# Revit family: Mirror-Acorn-LR1812-SLPT
name_source: partatom
category: Generic Models
units: mm (PartAtom-declared; Revit-internal decimal feet)

## family parameters
Can host rebar = No
Cut with Voids When Loaded = No
Host = Face
OmniClass Number = 23.40.95.17.17
OmniClass Title = Mirrors
Part Type = Normal
Room Calculation Point = No
Round Connector Dimension = Use Diameter
Shared = Yes

## types (1)
- LR1812-SLPT
    ADA Compliant = Yes
    Assembly Code = E2010
    Default Elevation = 0"
    Description = Secur-Care® Ligature-Resistant, Stainless Steel Security Mirror
    EG - Enviro-Glaze = No
    Finish = Stainless Steel-Acorn-Satin
    Height = 23 3/8"
    Installation Type = Wall Mounted
    Length = 13"
    Manufacturer = Acorn Engineering
    Material = Stainless Steel-Acorn-Satin
    Model = LR1812-SLPT
    Product Documentation Link = https://www.acorneng.com
    Product Page URL = https://www.acorneng.com
    SW - Wall Sleeve = No
    URL = https://www.acorneng.com
    Width = 5/8"

## geometry (parser evidence)
native form markers: Sweep x3
no freeform markers — native parametric forms only
